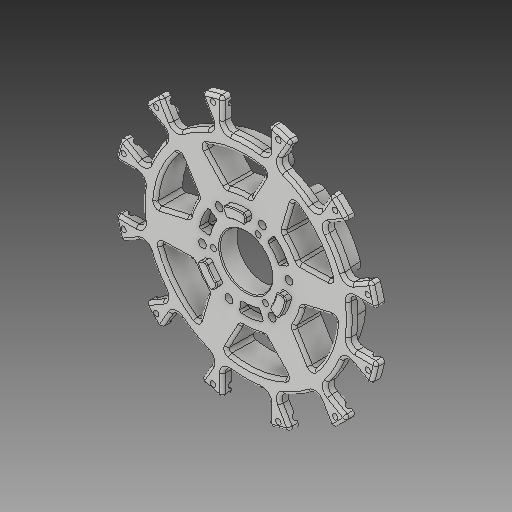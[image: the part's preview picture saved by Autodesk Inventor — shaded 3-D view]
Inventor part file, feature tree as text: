
AUTODESK INVENTOR PART (.ipt)
format: ipt  version: 2018 (Build 220112000, 112)  size: 1,297,920 bytes
history: native  units: in
note: dims shown in document units (in); Inventor stores cm internally (conversion verified against a paired STEP export)
features: chamfer x1
ambient origin geometry x8: Origin, YZ Plane, XZ Plane, XY Plane, X Axis, Y Axis, Z Axis, Center Point
bodies: Solid1 (feature_tree)
feature tree (1):
  chamfer  "Chamfer1"  [1 undecoded]
note: 1 required parameter value undecoded (feature->parameter linkage not recoverable at this tier; creation-order binding heuristic only, values carry confidence <= 0.55)
